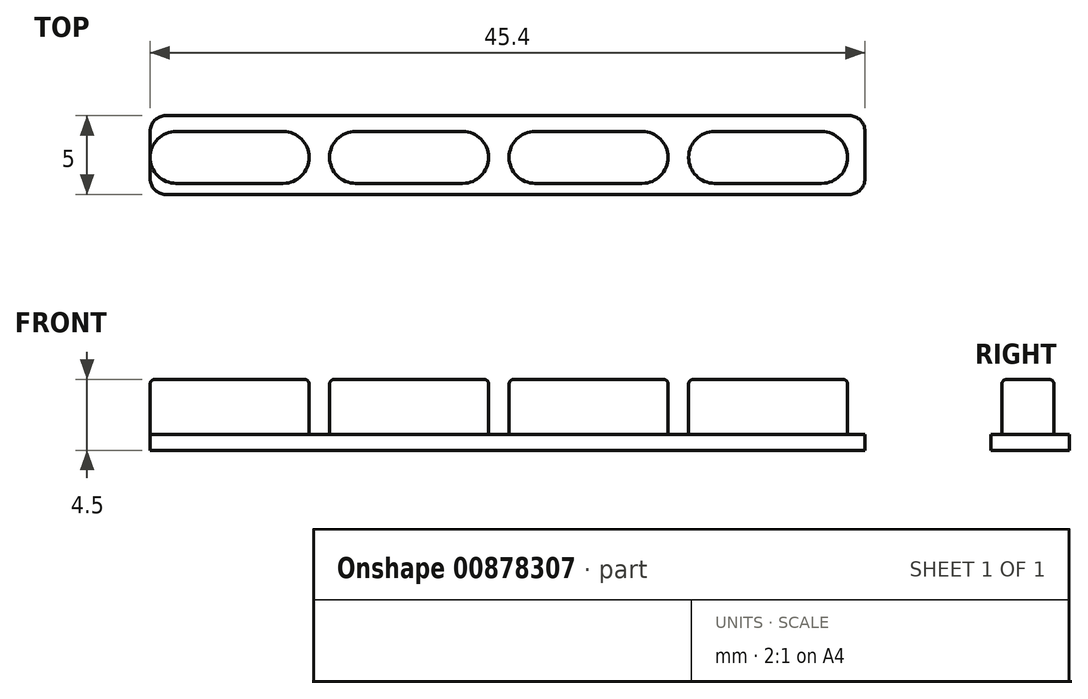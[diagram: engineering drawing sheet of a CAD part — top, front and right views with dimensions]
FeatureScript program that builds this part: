
annotation { "Feature Type Name" : "Feature", "Feature Type Description" : "" }
export const myFeature = defineFeature(function(context is Context, id is Id, definition is map)
    precondition{}
    {
        {
            var Q0;
            Q0=qCreatedBy(makeId("Top.planeOp"),FACE);
            var sketch = newSketch(context, id + "F0", { "sketchPlane" : qUnion([Q0])});
            skLineSegment(sketch, "E0.bottom", {"start": v(-18, -1.53) * mm, "end": v(27.4, -1.53) * mm});
            skLineSegment(sketch, "E0.top", {"start": v(-18, -6.53) * mm, "end": v(27.4, -6.53) * mm});
            skLineSegment(sketch, "E1", {"start": v(-18, -1.53) * mm, "end": v(-18, -6.53) * mm});
            skLineSegment(sketch, "E2", {"start": v(27.4, -1.53) * mm, "end": v(27.4, -6.53) * mm});
            skSolve(sketch);
        }
        {
            var Q0;
            Q0 = qSketchRegion(id + "F0", true);
            var Q1;
            Q1=makeQuery(id+"F0.imprint","IMPRINT",FACE,{"disambiguationData":[TD([[makeQuery(id+"F0.imprint","IMPRINT",EDGE,{"derivedFrom":sQuery(id+"F0.wireOp",EDGE,"E0.bottom")}),-1.0]])]});
            extrude(context, id + "F1", {"entities" : qUnion([Q0, Q1]), "depth" : 1 * mm, "offsetDistance" : 25 * mm});
        }
        {
            var Q0;
            Q0=makeQuery(id+"F1.opExtrude","CAP_FACE",FACE,{"disambiguationData":[OSD([sQuery(id+"F0.wireOp",EDGE,"E0.bottom"),sQuery(id+"F0.wireOp",EDGE,"E0.top"),sQuery(id+"F0.wireOp",EDGE,"CAc0TaKW-FZpv-nwAS-jl2J-yohHpJzjtUaa"),sQuery(id+"F0.wireOp",EDGE,"E8Y6aopH-YvoP-Wnqq-8dG4-MbJ7owvIaNYU")])],"isStart":false});
            var sketch = newSketch(context, id + "F2", { "sketchPlane" : qUnion([Q0])});
            skLineSegment(sketch, "E3.bottom", {"start": v(-16.35, -2.53) * mm, "end": v(-9.55, -2.53) * mm});
            skLineSegment(sketch, "E3.top", {"start": v(-16.35, -5.83) * mm, "end": v(-9.55, -5.83) * mm});
            skLineSegment(sketch, "E3.left", {"start": v(-16.35, -2.53) * mm, "end": v(-16.35, -5.83) * mm});
            skLineSegment(sketch, "E3.right", {"start": v(-9.55, -2.53) * mm, "end": v(-9.55, -5.83) * mm});
            skArc(sketch, "E4", {"start": v(-16.35, -2.53) * mm, "mid": v(-18, -4.18) * mm, "end": v(-16.35, -5.83) * mm});
            skArc(sketch, "E5", {"start": v(-9.55, -5.83) * mm, "mid": v(-7.9, -4.18) * mm, "end": v(-9.55, -2.53) * mm});
            skLineSegment(sketch, "E6.1.0.0", {"start": v(-4.95, -2.53) * mm, "end": v(1.85, -2.53) * mm});
            skArc(sketch, "E6.1.0.1", {"start": v(1.85, -5.83) * mm, "mid": v(3.5, -4.18) * mm, "end": v(1.85, -2.53) * mm});
            skLineSegment(sketch, "E6.1.0.2", {"start": v(1.85, -2.53) * mm, "end": v(1.85, -5.83) * mm});
            skLineSegment(sketch, "E6.1.0.3", {"start": v(-4.95, -5.83) * mm, "end": v(1.85, -5.83) * mm});
            skArc(sketch, "E6.1.0.4", {"start": v(-4.95, -2.53) * mm, "mid": v(-6.6, -4.18) * mm, "end": v(-4.95, -5.83) * mm});
            skLineSegment(sketch, "E6.1.0.5", {"start": v(-4.95, -2.53) * mm, "end": v(-4.95, -5.83) * mm});
            skLineSegment(sketch, "E6.2.0.0", {"start": v(6.45, -2.53) * mm, "end": v(13.25, -2.53) * mm});
            skArc(sketch, "E6.2.0.1", {"start": v(13.25, -5.83) * mm, "mid": v(14.9, -4.18) * mm, "end": v(13.25, -2.53) * mm});
            skLineSegment(sketch, "E6.2.0.2", {"start": v(13.25, -2.53) * mm, "end": v(13.25, -5.83) * mm});
            skLineSegment(sketch, "E6.2.0.3", {"start": v(6.45, -5.83) * mm, "end": v(13.25, -5.83) * mm});
            skArc(sketch, "E6.2.0.4", {"start": v(6.45, -2.53) * mm, "mid": v(4.8, -4.18) * mm, "end": v(6.45, -5.83) * mm});
            skLineSegment(sketch, "E6.2.0.5", {"start": v(6.45, -2.53) * mm, "end": v(6.45, -5.83) * mm});
            skLineSegment(sketch, "E6.3.0.0", {"start": v(17.85, -2.53) * mm, "end": v(24.65, -2.53) * mm});
            skArc(sketch, "E6.3.0.1", {"start": v(24.65, -5.83) * mm, "mid": v(26.3, -4.18) * mm, "end": v(24.65, -2.53) * mm});
            skLineSegment(sketch, "E6.3.0.2", {"start": v(24.65, -2.53) * mm, "end": v(24.65, -5.83) * mm});
            skLineSegment(sketch, "E6.3.0.3", {"start": v(17.85, -5.83) * mm, "end": v(24.65, -5.83) * mm});
            skArc(sketch, "E6.3.0.4", {"start": v(17.85, -2.53) * mm, "mid": v(16.2, -4.18) * mm, "end": v(17.85, -5.83) * mm});
            skLineSegment(sketch, "E6.3.0.5", {"start": v(17.85, -2.53) * mm, "end": v(17.85, -5.83) * mm});
            skLineSegment(sketch, "E6.direction1", {"start": v(-16.35, -2.53) * mm, "end": v(-4.95, -2.53) * mm, "construction": true});
            skSolve(sketch);
        }
        {
            var Q0;
            Q0=makeQuery(id+"F2.imprint","IMPRINT",FACE,{"disambiguationData":[TD([[makeQuery(id+"F2.imprint","IMPRINT",EDGE,{"derivedFrom":sQuery(id+"F2.wireOp",EDGE,"E3.bottom")}),-1.0]])]});
            var Q1;
            {var subQ0=sQuery(id+"F2.wireOp",EDGE,"E3.left");Q1=makeQuery(id+"F2.imprint","IMPRINT",FACE,{"disambiguationData":[TD([[makeQuery(id+"F2.imprint","IMPRINT",EDGE,{"derivedFrom":subQ0}),-1.0]])]});}
            var Q2;
            Q2=makeQuery(id+"F2.imprint","IMPRINT",FACE,{"disambiguationData":[TD([[makeQuery(id+"F2.imprint","IMPRINT",EDGE,{"derivedFrom":sQuery(id+"F2.wireOp",EDGE,"E3.right")}),1.0]])]});
            var Q3;
            Q3=makeQuery(id+"F2.imprint","IMPRINT",FACE,{"disambiguationData":[TD([[makeQuery(id+"F2.imprint","IMPRINT",EDGE,{"derivedFrom":sQuery(id+"F2.wireOp",EDGE,"E6.1.0.4")}),1.0]])]});
            var Q4;
            Q4=makeQuery(id+"F2.imprint","IMPRINT",FACE,{"disambiguationData":[TD([[makeQuery(id+"F2.imprint","IMPRINT",EDGE,{"derivedFrom":sQuery(id+"F2.wireOp",EDGE,"E6.1.0.0")}),-1.0]])]});
            var Q5;
            Q5=makeQuery(id+"F2.imprint","IMPRINT",FACE,{"disambiguationData":[TD([[makeQuery(id+"F2.imprint","IMPRINT",EDGE,{"derivedFrom":sQuery(id+"F2.wireOp",EDGE,"E6.1.0.1")}),1.0]])]});
            var Q6;
            Q6=makeQuery(id+"F2.imprint","IMPRINT",FACE,{"disambiguationData":[TD([[makeQuery(id+"F2.imprint","IMPRINT",EDGE,{"derivedFrom":sQuery(id+"F2.wireOp",EDGE,"E6.2.0.4")}),1.0]])]});
            var Q7;
            Q7=makeQuery(id+"F2.imprint","IMPRINT",FACE,{"disambiguationData":[TD([[makeQuery(id+"F2.imprint","IMPRINT",EDGE,{"derivedFrom":sQuery(id+"F2.wireOp",EDGE,"E6.2.0.0")}),-1.0]])]});
            var Q8;
            Q8=makeQuery(id+"F2.imprint","IMPRINT",FACE,{"disambiguationData":[TD([[makeQuery(id+"F2.imprint","IMPRINT",EDGE,{"derivedFrom":sQuery(id+"F2.wireOp",EDGE,"E6.2.0.1")}),1.0]])]});
            var Q9;
            Q9=makeQuery(id+"F2.imprint","IMPRINT",FACE,{"disambiguationData":[TD([[makeQuery(id+"F2.imprint","IMPRINT",EDGE,{"derivedFrom":sQuery(id+"F2.wireOp",EDGE,"E6.3.0.4")}),1.0]])]});
            var Q10;
            Q10=makeQuery(id+"F2.imprint","IMPRINT",FACE,{"disambiguationData":[TD([[makeQuery(id+"F2.imprint","IMPRINT",EDGE,{"derivedFrom":sQuery(id+"F2.wireOp",EDGE,"E6.3.0.0")}),-1.0]])]});
            var Q11;
            Q11=makeQuery(id+"F2.imprint","IMPRINT",FACE,{"disambiguationData":[TD([[makeQuery(id+"F2.imprint","IMPRINT",EDGE,{"derivedFrom":sQuery(id+"F2.wireOp",EDGE,"E6.3.0.1")}),1.0]])]});
            extrude(context, id + "F3", {"entities" : qUnion([Q0, Q1, Q2, Q3, Q4, Q5, Q6, Q7, Q8, Q9, Q10, Q11]), "operationType" : NewBodyOperationType.ADD, "depth" : 3.5 * mm, "offsetDistance" : 25 * mm});
        }
        {
            var Q0;
            Q0=makeQuery(id+"F1.opExtrude","SWEPT_EDGE",EDGE,{"disambiguationData":[OSD([sQuery(id+"F0.wireOp",EDGE,"E0.bottom"),sQuery(id+"F0.wireOp",EDGE,"E1")])]});
            var Q1;
            Q1=makeQuery(id+"F1.opExtrude","SWEPT_EDGE",EDGE,{"disambiguationData":[OSD([sQuery(id+"F0.wireOp",EDGE,"E0.top"),sQuery(id+"F0.wireOp",EDGE,"E1")])]});
            var Q2;
            Q2=makeQuery(id+"F1.opExtrude","SWEPT_EDGE",EDGE,{"disambiguationData":[OSD([sQuery(id+"F0.wireOp",EDGE,"E0.bottom"),sQuery(id+"F0.wireOp",EDGE,"E2")])]});
            var Q3;
            Q3=makeQuery(id+"F1.opExtrude","SWEPT_EDGE",EDGE,{"disambiguationData":[OSD([sQuery(id+"F0.wireOp",EDGE,"E0.top"),sQuery(id+"F0.wireOp",EDGE,"E2")])]});
            fillet(context, id + "F4", {"entities" : qUnion([Q0, Q1, Q2, Q3]), "radius" : 1 * mm, "tangentPropagation" : true, "allowEdgeOverflow" : false});
        }
        {
            var Q0;
            Q0=makeQuery(id+"F3.opExtrude","CAP_EDGE",EDGE,{"disambiguationData":[OSD([sQuery(id+"F2.wireOp",EDGE,"E4")])],"isStart":false});
            var Q1;
            Q1=makeQuery(id+"F3.opExtrude","CAP_EDGE",EDGE,{"disambiguationData":[OSD([sQuery(id+"F2.wireOp",EDGE,"E6.1.0.4")])],"isStart":false});
            var Q2;
            Q2=makeQuery(id+"F3.opExtrude","CAP_EDGE",EDGE,{"disambiguationData":[OSD([sQuery(id+"F2.wireOp",EDGE,"E6.2.0.4")])],"isStart":false});
            var Q3;
            Q3=makeQuery(id+"F3.opExtrude","CAP_EDGE",EDGE,{"disambiguationData":[OSD([sQuery(id+"F2.wireOp",EDGE,"E6.3.0.4")])],"isStart":false});
            fillet(context, id + "F5", {"entities" : qUnion([Q0, Q1, Q2, Q3]), "radius" : 0.3 * mm, "tangentPropagation" : true, "allowEdgeOverflow" : false});
        }
    });
